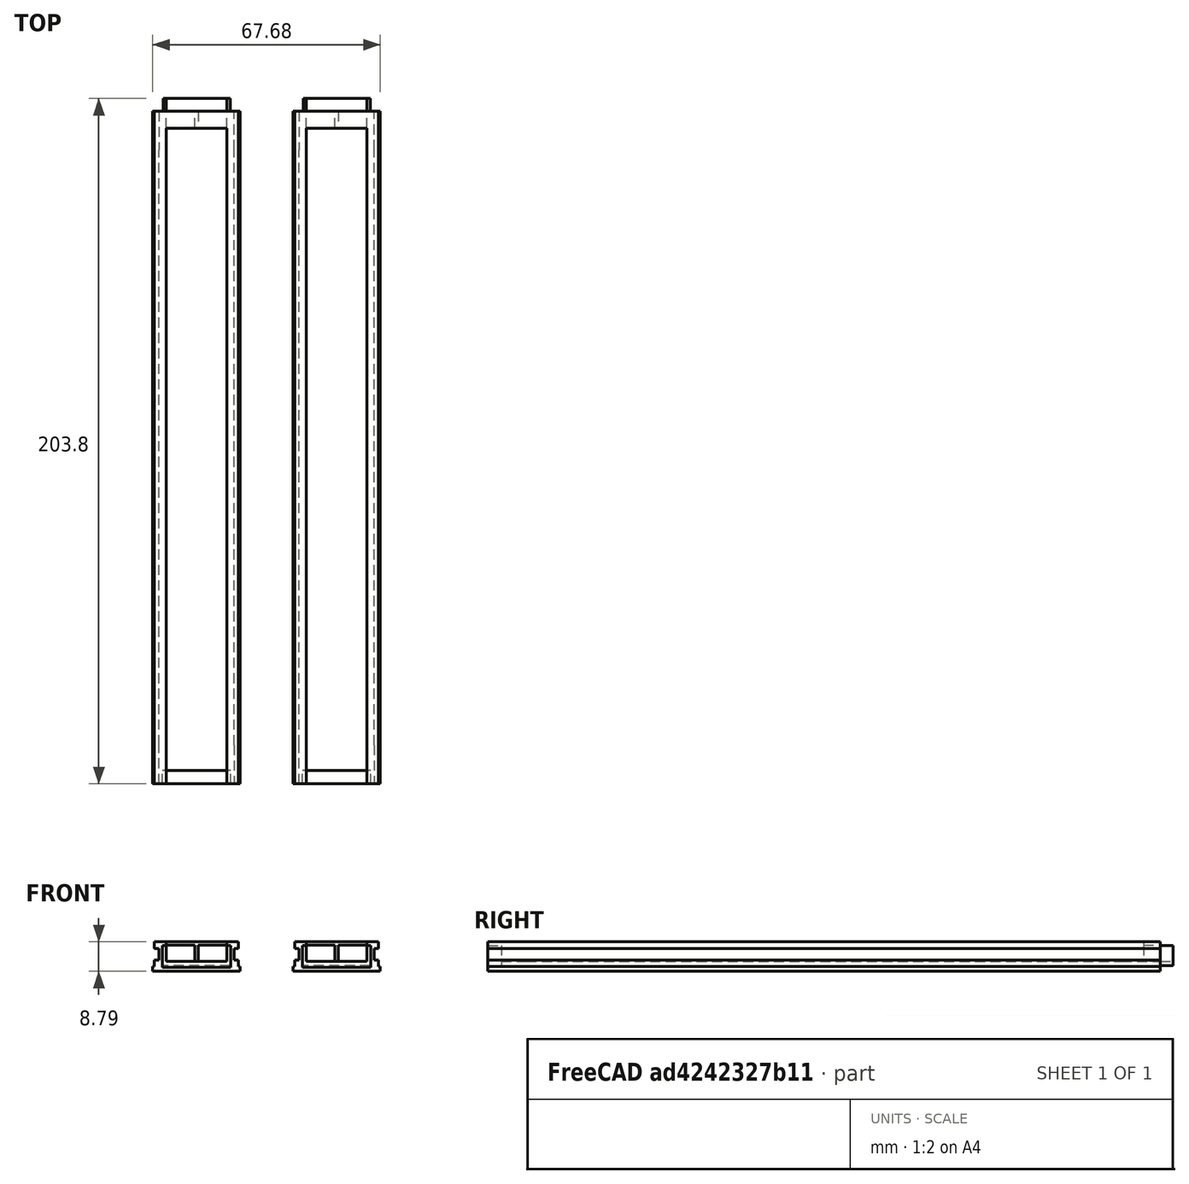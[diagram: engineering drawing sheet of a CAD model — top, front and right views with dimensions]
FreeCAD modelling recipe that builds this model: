
FCSTD DOCUMENT  (FreeCAD 0.18.3R)
Label: lamp.rail.20cm
License: All rights reserved
LicenseURL: http://en.wikipedia.org/wiki/All_rights_reserved
objects: Part::Feature×4, Part::Extrusion×3, Part::MultiFuse×3
note: 10 computed .brp shape members not serialized (recipe doc carries the construction recipe); baked Part::Feature solids carry a one-line shape summary decoded from their .brp

FEATURE [Part::Feature] Cut047_solid001  label="Cut047 (Solid)001"
  Placement = pos=(36.1596,254.509,-3.59e-14) rot=(0,0,1;0rad)
  shape: bbox 26 x 15.3 x 8.799 mm, 30 faces (baked)
FEATURE [Part::Feature] Cut037_solid001001  label="Cut037 (Solid)002"
  Placement = pos=(36.1596,-5.32723,-2.2e-15) rot=(0,0,1;0rad)
  shape: bbox 26 x 11.5 x 8.799 mm, 28 faces (baked)
FEATURE [Part::Extrusion] Extrusion038
  Dir = (8.3e-15,-2.72e-14,-4.79945)
  DirMode = 0
  FaceMakerClass = Part::FaceMakerBullseye
  LengthFwd = 0
  LengthRev = 0
  Solid = true
  Symmetric = false
FEATURE [Part::Extrusion] Extrusion039
  Dir = (18,0,0)
  DirMode = 0
  FaceMakerClass = Part::FaceMakerBullseye
  LengthFwd = 0
  LengthRev = 0
  Solid = true
  Symmetric = false
FEATURE [Part::MultiFuse] Fusion001
  Placement = pos=(24.4812,182.869,-4) rot=(0,0,1;0rad)
  Shapes = -> [Extrusion038,Extrusion039]
FEATURE [Part::MultiFuse] Fusion
  Placement = pos=(-7.11e-14,-50,2.89e-14) rot=(0,0,1;0rad)
  Shapes = -> [Cut047_solid001,Fusion001]
FEATURE [Part::Feature] Face001
  Placement = pos=(36.1596,-5.32723,-2e-15) rot=(0,0,1;0rad)
  shape: bbox 26 x 5.243e-07 x 8.799 mm, 1 faces, 0 solids (baked)
FEATURE [Part::Extrusion] Extrusion
  Base = -> Face001
  Dir = (6.02e-14,177,-4.25e-14)
  DirMode = 0
  FaceMakerClass = Part::FaceMakerBullseye
  LengthFwd = 0
  LengthRev = 0
  Solid = true
  Symmetric = false
FEATURE [Part::MultiFuse] Fusion002
  Shapes = -> [Cut037_solid001001,Fusion,Extrusion]
FEATURE [Part::Feature] Fusion002_solid  label="Fusion002 (Solid)"
  Placement = pos=(41.6811,0,-6.2e-15) rot=(0,0,1;0rad)
  shape: bbox 26 x 203.8 x 8.799 mm, 86 faces (baked)
